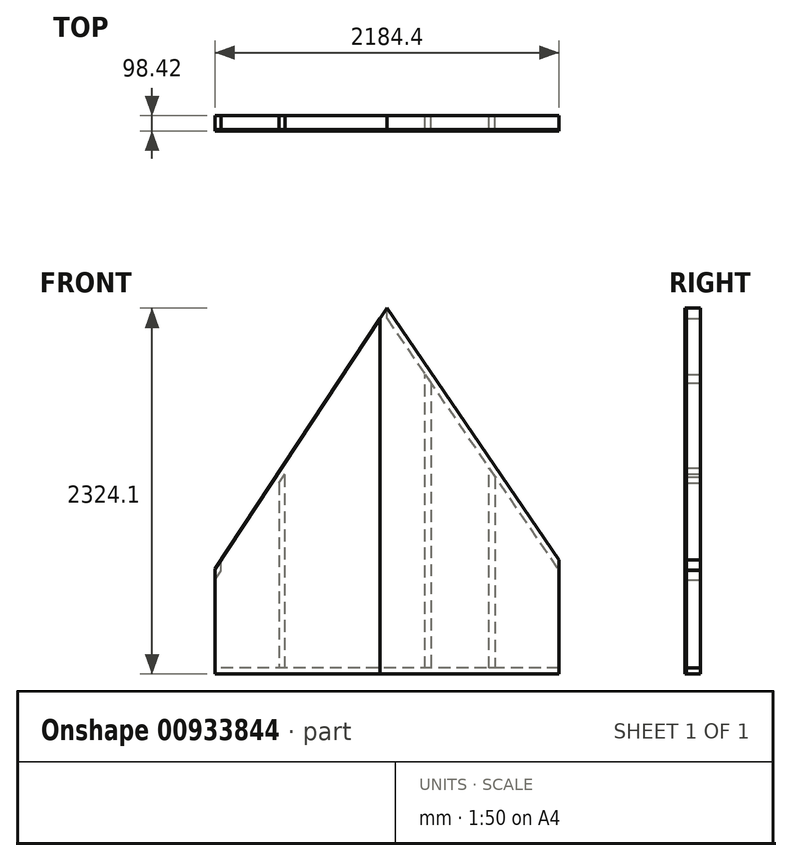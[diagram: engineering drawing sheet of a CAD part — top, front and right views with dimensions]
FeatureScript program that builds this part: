
annotation { "Feature Type Name" : "Feature", "Feature Type Description" : "" }
export const myFeature = defineFeature(function(context is Context, id is Id, definition is map)
    precondition{}
    {
        {
            var Q0;
            Q0=qCreatedBy(makeId("Front.planeOp"),FACE);
            var sketch = newSketch(context, id + "F0", { "sketchPlane" : qUnion([Q0])});
            skLineSegment(sketch, "E0.bottom", {"start": v(1092.2, -19.05) * mm, "end": v(-1092.2, -19.05) * mm});
            skLineSegment(sketch, "E0.top", {"start": v(1092.2, 19.05) * mm, "end": v(-1092.2, 19.05) * mm});
            skLineSegment(sketch, "E0.left", {"start": v(1092.2, -19.05) * mm, "end": v(1092.2, 19.05) * mm});
            skLineSegment(sketch, "E0.right", {"start": v(-1092.2, -19.05) * mm, "end": v(-1092.2, 19.05) * mm});
            skPoint(sketch, "E0.middle", {"position": v(0, 0) * mm});
            skLineSegment(sketch, "E1.bottom", {"start": v(-1054.1, 19.05) * mm, "end": v(-1092.2, 19.05) * mm});
            skLineSegment(sketch, "E1.top", {"start": v(-1054.1, 704.85) * mm, "end": v(-1092.2, 704.85) * mm});
            skLineSegment(sketch, "E1.left", {"start": v(-1054.1, 19.05) * mm, "end": v(-1054.1, 704.85) * mm});
            skLineSegment(sketch, "E1.right", {"start": v(-1092.2, 19.05) * mm, "end": v(-1092.2, 704.85) * mm});
            skLineSegment(sketch, "E2.bottom", {"start": v(1054.1, 19.05) * mm, "end": v(1092.2, 19.05) * mm});
            skLineSegment(sketch, "E2.top", {"start": v(1054.1, 704.85) * mm, "end": v(1092.2, 704.85) * mm});
            skLineSegment(sketch, "E2.left", {"start": v(1054.1, 19.05) * mm, "end": v(1054.1, 704.85) * mm});
            skLineSegment(sketch, "E2.right", {"start": v(1092.2, 19.05) * mm, "end": v(1092.2, 704.85) * mm});
            skLineSegment(sketch, "E3.bottom", {"start": v(-88.9, 19.05) * mm, "end": v(0, 19.05) * mm});
            skLineSegment(sketch, "E3.top", {"start": v(-88.9, 2305.05) * mm, "end": v(0, 2305.05) * mm});
            skLineSegment(sketch, "E3.left", {"start": v(-88.9, 19.05) * mm, "end": v(-88.9, 2305.05) * mm});
            skLineSegment(sketch, "E3.right", {"start": v(0, 19.05) * mm, "end": v(0, 2305.05) * mm});
            skLineSegment(sketch, "E4", {"start": v(0, 2305.05) * mm, "end": v(-1054.1, 704.85) * mm, "construction": true});
            skLineSegment(sketch, "E5", {"start": v(0, 2305.05) * mm, "end": v(1092.2, 704.85) * mm, "construction": true});
            skLineSegment(sketch, "E6", {"start": v(-1054.1, 704.85) * mm, "end": v(-1092.2, 647.01) * mm});
            skLineSegment(sketch, "E7", {"start": v(-1092.2, 647.01) * mm, "end": v(-1054.1, 704.85) * mm});
            skLineSegment(sketch, "E8", {"start": v(0, 2305.05) * mm, "end": v(-1054.1, 704.85) * mm});
            skLineSegment(sketch, "E9", {"start": v(-1092.2, 577.75) * mm, "end": v(-88.9, 2100.83) * mm});
            skLineSegment(sketch, "E10", {"start": v(-88.9, 2100.83) * mm, "end": v(-88.9, 2170.1) * mm});
            skLineSegment(sketch, "E11", {"start": v(-88.9, 2170.1) * mm, "end": v(-1092.2, 647.01) * mm});
            skLineSegment(sketch, "E12", {"start": v(0, 2305.05) * mm, "end": v(1092.2, 704.85) * mm});
            skLineSegment(sketch, "E13", {"start": v(-562.3, 3061.3) * mm, "end": v(1857.7, -484.27) * mm, "construction": true});
            skLineSegment(sketch, "E14", {"start": v(0, 2237.47) * mm, "end": v(1092.2, 637.27) * mm});
            skLineSegment(sketch, "E15.bottom", {"start": v(-685.8, 1375.8) * mm, "end": v(-647.7, 1375.8) * mm, "construction": true});
            skLineSegment(sketch, "E15.top", {"start": v(-685.8, -711.6) * mm, "end": v(-647.7, -711.6) * mm, "construction": true});
            skLineSegment(sketch, "E15.left", {"start": v(-685.8, 1375.8) * mm, "end": v(-685.8, -711.6) * mm, "construction": true});
            skLineSegment(sketch, "E15.right", {"start": v(-647.7, 1375.8) * mm, "end": v(-647.7, -711.6) * mm, "construction": true});
            skLineSegment(sketch, "E16.bottom", {"start": v(-279.4, 2044.01) * mm, "end": v(-241.3, 2044.01) * mm, "construction": true});
            skLineSegment(sketch, "E16.top", {"start": v(-279.4, -635.22) * mm, "end": v(-241.3, -635.22) * mm, "construction": true});
            skLineSegment(sketch, "E16.left", {"start": v(-279.4, 2044.01) * mm, "end": v(-279.4, -635.22) * mm, "construction": true});
            skLineSegment(sketch, "E16.right", {"start": v(-241.3, 2044.01) * mm, "end": v(-241.3, -635.22) * mm, "construction": true});
            skLineSegment(sketch, "E17.bottom", {"start": v(279.4, 1700.36) * mm, "end": v(241.3, 1700.36) * mm, "construction": true});
            skLineSegment(sketch, "E17.top", {"start": v(279.4, -883.42) * mm, "end": v(241.3, -883.42) * mm, "construction": true});
            skLineSegment(sketch, "E17.left", {"start": v(279.4, 1700.36) * mm, "end": v(279.4, -883.42) * mm, "construction": true});
            skLineSegment(sketch, "E17.right", {"start": v(241.3, 1700.36) * mm, "end": v(241.3, -883.42) * mm, "construction": true});
            skLineSegment(sketch, "E18.bottom", {"start": v(647.7, 1350.34) * mm, "end": v(685.8, 1350.34) * mm, "construction": true});
            skLineSegment(sketch, "E18.top", {"start": v(647.7, -1029.8) * mm, "end": v(685.8, -1029.8) * mm, "construction": true});
            skLineSegment(sketch, "E18.left", {"start": v(647.7, 1350.34) * mm, "end": v(647.7, -1029.8) * mm, "construction": true});
            skLineSegment(sketch, "E18.right", {"start": v(685.8, 1350.34) * mm, "end": v(685.8, -1029.8) * mm, "construction": true});
            skLineSegment(sketch, "E19", {"start": v(241.3, 19.05) * mm, "end": v(241.3, 1883.93) * mm});
            skLineSegment(sketch, "E20", {"start": v(241.3, 1883.93) * mm, "end": v(279.4, 1828.11) * mm});
            skLineSegment(sketch, "E21", {"start": v(279.4, 1828.11) * mm, "end": v(279.4, 19.05) * mm});
            skLineSegment(sketch, "E22", {"start": v(279.4, 19.05) * mm, "end": v(241.3, 19.05) * mm});
            skLineSegment(sketch, "E23", {"start": v(647.7, 19.05) * mm, "end": v(647.7, 1288.51) * mm});
            skLineSegment(sketch, "E24", {"start": v(647.7, 1288.51) * mm, "end": v(685.8, 1232.69) * mm});
            skLineSegment(sketch, "E25", {"start": v(685.8, 1232.69) * mm, "end": v(685.8, 19.05) * mm});
            skLineSegment(sketch, "E26", {"start": v(685.8, 19.05) * mm, "end": v(647.7, 19.05) * mm});
            skLineSegment(sketch, "E27", {"start": v(-685.8, 1194.7) * mm, "end": v(-685.8, 19.05) * mm});
            skLineSegment(sketch, "E28", {"start": v(-685.8, 19.05) * mm, "end": v(-647.7, 19.05) * mm});
            skLineSegment(sketch, "E29", {"start": v(-647.7, 19.05) * mm, "end": v(-647.7, 1252.53) * mm});
            skLineSegment(sketch, "E30", {"start": v(-647.7, 1252.53) * mm, "end": v(-685.8, 1194.7) * mm});
            skLineSegment(sketch, "E31", {"start": v(-279.4, 19.05) * mm, "end": v(-241.3, 19.05) * mm});
            skLineSegment(sketch, "E32", {"start": v(-241.3, 19.05) * mm, "end": v(-241.3, 1869.48) * mm});
            skLineSegment(sketch, "E33", {"start": v(-241.3, 1869.48) * mm, "end": v(-279.4, 1811.64) * mm});
            skLineSegment(sketch, "E34", {"start": v(-279.4, 1811.64) * mm, "end": v(-279.4, 19.05) * mm});
            skSolve(sketch);
        }
        {
            var Q0;
            {var subQ0=sQuery(id+"F0.wireOp",EDGE,"E1.bottom");Q0=makeQuery(id+"F0.imprint","IMPRINT",FACE,{"disambiguationData":[TD([[makeQuery(id+"F0.imprint","IMPRINT",EDGE,{"derivedFrom":subQ0}),-1.0]])]});}
            var Q1;
            Q1=makeQuery(id+"F0.imprint","IMPRINT",FACE,{"disambiguationData":[TD([[makeQuery(id+"F0.imprint","IMPRINT",EDGE,{"derivedFrom":sQuery(id+"F0.wireOp",EDGE,"E27")}),1.0]])]});
            var Q2;
            Q2=makeQuery(id+"F0.imprint","IMPRINT",FACE,{"disambiguationData":[TD([[makeQuery(id+"F0.imprint","IMPRINT",EDGE,{"derivedFrom":sQuery(id+"F0.wireOp",EDGE,"E31")}),1.0]])]});
            var Q3;
            {var subQ1=sQuery(id+"F0.wireOp",EDGE,"E3.bottom");Q3=makeQuery(id+"F0.imprint","IMPRINT",FACE,{"disambiguationData":[TD([[makeQuery(id+"F0.imprint","IMPRINT",EDGE,{"derivedFrom":subQ1}),1.0]])]});}
            var Q4;
            Q4=makeQuery(id+"F0.imprint","IMPRINT",FACE,{"disambiguationData":[TD([[makeQuery(id+"F0.imprint","IMPRINT",EDGE,{"derivedFrom":sQuery(id+"F0.wireOp",EDGE,"E19")}),-1.0]])]});
            var Q5;
            Q5=makeQuery(id+"F0.imprint","IMPRINT",FACE,{"disambiguationData":[TD([[makeQuery(id+"F0.imprint","IMPRINT",EDGE,{"derivedFrom":sQuery(id+"F0.wireOp",EDGE,"E23")}),-1.0]])]});
            var Q6;
            {var subQ0=sQuery(id+"F0.wireOp",EDGE,"E2.bottom");Q6=makeQuery(id+"F0.imprint","IMPRINT",FACE,{"disambiguationData":[TD([[makeQuery(id+"F0.imprint","IMPRINT",EDGE,{"derivedFrom":subQ0}),1.0]])]});}
            extrude(context, id + "F1", {"entities" : qUnion([Q0, Q1, Q2, Q3, Q4, Q5, Q6]), "depth" : 88.9 * mm, "offsetDistance" : 25.4 * mm});
        }
        {
            var Q0;
            {var subQ5=sQuery(id+"F0.wireOp",EDGE,"E10");Q0=makeQuery(id+"F0.imprint","IMPRINT",FACE,{"disambiguationData":[TD([[makeQuery(id+"F0.imprint","IMPRINT",EDGE,{"derivedFrom":subQ5}),1.0]])]});}
            var Q1;
            {var subQ3=sQuery(id+"F0.wireOp",EDGE,"E9");var subQ5=sQuery(id+"F0.wireOp",EDGE,"E1.right");var subQ6=makeQuery(id+"F0.imprint","INTERSECT",VERTEX,{"derivedFrom":[subQ5,subQ3]});Q1=makeQuery(id+"F0.imprint","IMPRINT",FACE,{"disambiguationData":[TD([[makeQuery(id+"F0.imprint","IMPRINT",EDGE,{"disambiguationData":[TD([[subQ6,-1.0]])],"derivedFrom":subQ5}),-1.0]])]});}
            var Q2;
            {var subQ2=sQuery(id+"F0.wireOp",EDGE,"E2.top");Q2=makeQuery(id+"F0.imprint","IMPRINT",FACE,{"disambiguationData":[TD([[makeQuery(id+"F0.imprint","IMPRINT",EDGE,{"derivedFrom":subQ2}),1.0]])]});}
            var Q3;
            {var subQ0=sQuery(id+"F0.wireOp",EDGE,"E2.top");Q3=makeQuery(id+"F0.imprint","IMPRINT",FACE,{"disambiguationData":[TD([[makeQuery(id+"F0.imprint","IMPRINT",EDGE,{"derivedFrom":subQ0}),-1.0]])]});}
            var Q4;
            Q4=makeQuery(id+"F0.imprint","IMPRINT",FACE,{"disambiguationData":[TD([[makeQuery(id+"F0.imprint","IMPRINT",EDGE,{"derivedFrom":sQuery(id+"F0.wireOp",EDGE,"E0.bottom")}),-1.0]])]});
            extrude(context, id + "F2", {"entities" : qUnion([Q0, Q1, Q2, Q3, Q4]), "depth" : 88.9 * mm, "offsetDistance" : 25.4 * mm});
        }
        {
            var Q0;
            Q0=makeQuery(id+"F2.opExtrude","CAP_FACE",FACE,{"disambiguationData":[OSD([sQuery(id+"F0.wireOp",EDGE,"E0.bottom"),sQuery(id+"F0.wireOp",EDGE,"E0.top"),sQuery(id+"F0.wireOp",EDGE,"E0.left"),sQuery(id+"F0.wireOp",EDGE,"E0.right"),sQuery(id+"F0.wireOp",EDGE,"E1.bottom"),sQuery(id+"F0.wireOp",EDGE,"E2.bottom"),sQuery(id+"F0.wireOp",EDGE,"E3.bottom"),sQuery(id+"F0.wireOp",EDGE,"E22"),sQuery(id+"F0.wireOp",EDGE,"E26"),sQuery(id+"F0.wireOp",EDGE,"E28"),sQuery(id+"F0.wireOp",EDGE,"E31")])],"isStart":false});
            var sketch = newSketch(context, id + "F3", { "sketchPlane" : qUnion([Q0])});
            skLineSegment(sketch, "E35.0", {"start": v(-1092.2, 19.05) * mm, "end": v(-1092.2, 577.75) * mm});
            skLineSegment(sketch, "E36.0", {"start": v(-88.9, 2170.1) * mm, "end": v(-1092.2, 647.01) * mm});
            skLineSegment(sketch, "E37.0", {"start": v(-1092.2, 577.75) * mm, "end": v(-1092.2, 647.01) * mm});
            skLineSegment(sketch, "E38.0", {"start": v(-1092.2, -19.05) * mm, "end": v(-1092.2, 19.05) * mm});
            skLineSegment(sketch, "E39.0", {"start": v(1092.2, -19.05) * mm, "end": v(-1092.2, -19.05) * mm});
            skLineSegment(sketch, "E40.0", {"start": v(0, 2305.05) * mm, "end": v(-88.9, 2170.1) * mm});
            skLineSegment(sketch, "E41.0", {"start": v(0, 2305.05) * mm, "end": v(1092.2, 704.85) * mm});
            skLineSegment(sketch, "E42.0", {"start": v(1092.2, 637.27) * mm, "end": v(1092.2, 704.85) * mm});
            skLineSegment(sketch, "E43.0", {"start": v(1092.2, 19.05) * mm, "end": v(1092.2, 637.27) * mm});
            skPoint(sketch, "E44.0", {"position": v(-44.45, 19.05) * mm});
            skLineSegment(sketch, "E45.0.0", {"start": v(-88.9, 2170.1) * mm, "end": v(-88.9, 19.05) * mm});
            skLineSegment(sketch, "E45.0.1", {"start": v(-88.9, 19.05) * mm, "end": v(0, 19.05) * mm});
            skLineSegment(sketch, "E45.0.2", {"start": v(0, 19.05) * mm, "end": v(0, 2305.05) * mm});
            skLineSegment(sketch, "E46", {"start": v(-44.45, 19.05) * mm, "end": v(-44.45, 2237.57) * mm});
            skLineSegment(sketch, "E47", {"start": v(-44.45, 19.05) * mm, "end": v(-44.45, -19.05) * mm});
            skSolve(sketch);
        }
        {
            var Q0;
            {var subQ2=sQuery(id+"F3.wireOp",EDGE,"E38.0");Q0=makeQuery(id+"F3.imprint","IMPRINT",FACE,{"disambiguationData":[TD([[makeQuery(id+"F3.imprint","IMPRINT",EDGE,{"derivedFrom":subQ2}),-1.0]])]});}
            var Q1;
            {var subQ1=sQuery(id+"F3.wireOp",EDGE,"E35.0");Q1=makeQuery(id+"F3.imprint","IMPRINT",FACE,{"disambiguationData":[TD([[makeQuery(id+"F3.imprint","IMPRINT",EDGE,{"derivedFrom":subQ1}),-1.0]])]});}
            var Q2;
            {var subQ0=sQuery(id+"F3.wireOp",EDGE,"E45.0.0");Q2=makeQuery(id+"F3.imprint","IMPRINT",FACE,{"disambiguationData":[TD([[makeQuery(id+"F3.imprint","IMPRINT",EDGE,{"derivedFrom":subQ0}),1.0]])]});}
            extrude(context, id + "F4", {"entities" : qUnion([Q0, Q1, Q2]), "depth" : 9.52 * mm, "offsetDistance" : 25.4 * mm});
        }
        {
            var Q0;
            Q0=makeQuery(id+"F3.imprint","IMPRINT",FACE,{"disambiguationData":[TD([[makeQuery(id+"F3.imprint","IMPRINT",EDGE,{"derivedFrom":sQuery(id+"F3.wireOp",EDGE,"E41.0")}),-1.0]])]});
            var Q1;
            {var subQ1=sQuery(id+"F3.wireOp",EDGE,"E47");Q1=makeQuery(id+"F3.imprint","IMPRINT",FACE,{"disambiguationData":[TD([[makeQuery(id+"F3.imprint","IMPRINT",EDGE,{"derivedFrom":subQ1}),1.0]])]});}
            var Q2;
            {var subQ0=sQuery(id+"F3.wireOp",EDGE,"E45.0.2");Q2=makeQuery(id+"F3.imprint","IMPRINT",FACE,{"disambiguationData":[TD([[makeQuery(id+"F3.imprint","IMPRINT",EDGE,{"derivedFrom":subQ0}),1.0]])]});}
            extrude(context, id + "F5", {"entities" : qUnion([Q0, Q1, Q2]), "depth" : 9.52 * mm, "offsetDistance" : 25.4 * mm});
        }
    });
